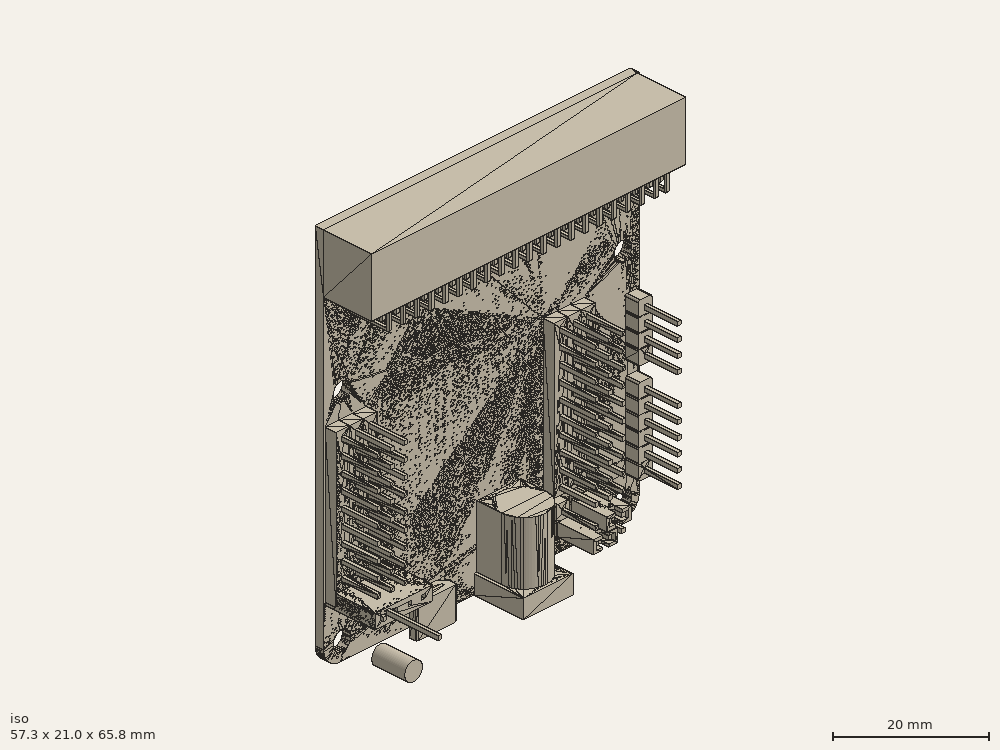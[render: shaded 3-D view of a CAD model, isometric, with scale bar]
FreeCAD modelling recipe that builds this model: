
FCSTD DOCUMENT  (FreeCAD 0.20R29603 (Git))
Label: PlacaExpansion
License: All rights reserved
LicenseURL: http://en.wikipedia.org/wiki/All_rights_reserved
objects: Part::Box×66, Part::MultiFuse×27, Part::Fillet×22, Part::FeaturePython×16, Part::Cut×16, Part::Cylinder×8, Part::Chamfer×8
note: 147 computed .brp shape members not serialized (recipe doc carries the construction recipe); baked Part::Feature solids carry a one-line shape summary decoded from their .brp

FEATURE [Part::Box] Box103  label="Extensor002"
  AttacherType = Attacher::AttachEngine3D
  Height = 65.33
  Length = 1.54
  Placement = pos=(30,-28,3) rot=(0,0,1;1.5708rad)
  Width = 57.33
FEATURE [Part::Box] Box202  label="Cubo189"
  AttacherType = Attacher::AttachEngine3D
  Height = 10
  Length = 57
  Placement = pos=(-27.33,-36.75,58.33) rot=(0,0,1;0rad)
  Width = 8.8
FEATURE [Part::Box] Box207  label="Cubo194"
  AttacherType = Attacher::AttachEngine3D
  Height = 26
  Length = 2.5
  Placement = pos=(-27,-30,13) rot=(0,0,1;0rad)
  Width = 2.5
FEATURE [Part::Box] Box208  label="Cubo195"
  AttacherType = Attacher::AttachEngine3D
  Height = 26
  Length = 2.5
  Placement = pos=(-24.5,-30,13) rot=(0,0,1;0rad)
  Width = 2.5
FEATURE [Part::Box] Box209  label="Cubo196"
  AttacherType = Attacher::AttachEngine3D
  Height = 26
  Length = 2.5
  Placement = pos=(-22,-30,13) rot=(0,0,1;0rad)
  Width = 2.5
FEATURE [Part::Box] Box210  label="Cubo197"
  AttacherType = Attacher::AttachEngine3D
  Height = 11
  Length = 0.6
  Placement = pos=(-26,-25.5,14) rot=(1,0,0;1.5708rad)
  Width = 0.7
FEATURE [Part::FeaturePython] Array003  # Draft array (typed FeaturePython)
  AlwaysSyncPlacement = false
  Angle = 360
  ArrayType = 0
  Axis = (0,0,1)
  Base = -> Box210
  Center = (0,0,0)
  Count = 30
  ExpandArray = false
  Fuse = false
  IntervalAxis = (0,0,0)
  IntervalX = (2.45,0,0)
  IntervalY = (0,100,0)
  IntervalZ = (0,0,2.6)
  NumberCircles = 3
  NumberPolar = 5
  NumberX = 3
  NumberY = 1
  NumberZ = 10
  PlacementList = 30 placements: [(-26,-25.5,14),(-26,-25.5,16.6),(-26,-25.5,19.2),(-26,-25.5,21.8),(-26,-25.5,24.4),(-26,-25.5,27),(-26,-25.5,29.6),(-26,-25.5,32.2),(-26,-25.5,34.8),(-26,-25.5,37.4),(-23.55,-25.5,14),(-23.55,-25.5,16.6),(-23.55,-25.5,19.2),(-23.55,-25.5,21.8),(-23.55,-25.5,24.4),(-23.55,-25.5,27),(-23.55,-25.5,29.6),(-23.55,-25.5,32.2),(-23.55,-25.5,34.8),(-23.55,-25.5,37.4),(-21.1,-25.5,14),(-21.1,-25.5,16.6),+8 more]
  RadialDistance = 50
  ScaleList = (30) [(1,1,1),(1,1,1),(1,1,1),(1,1,1),(1,1,1),(1,1,1),(1,1,1),(1,1,1),(1,1,1),(1,1,1),(1,1,1),(1,1,1),(1,1,1),(1,1,1),(1,1,1),(1,1,1),(1,1,1),(1,1,1),+12 more]
  Symmetry = 1
  TangentialDistance = 25
FEATURE [Part::Cylinder] Cylinder189  label="Cilindro189"
  Angle = 360
  AttacherType = Attacher::AttachEngine3D
  FirstAngle = 0
  Height = 6
  Placement = pos=(-24,-24,6) rot=(1,0,0;1.5708rad)
  Radius = 1.6
  SecondAngle = 0
FEATURE [Part::FeaturePython] Array001  # Draft array (typed FeaturePython)
  AlwaysSyncPlacement = false
  Angle = 360
  ArrayType = 0
  Axis = (0,0,1)
  Base = -> Cylinder189
  Center = (0,0,0)
  Count = 4
  ExpandArray = false
  Fuse = false
  IntervalAxis = (0,0,0)
  IntervalX = (51,0,0)
  IntervalY = (0,100,0)
  IntervalZ = (0,0,37)
  NumberCircles = 3
  NumberPolar = 5
  NumberX = 2
  NumberY = 1
  NumberZ = 2
  PlacementList = 4 placements: [(-24,-24,6),(-24,-24,43),(27,-24,6),(27,-24,43)]
  RadialDistance = 50
  ScaleList = (4) [(1,1,1),(1,1,1),(1,1,1),(1,1,1)]
  Symmetry = 1
  TangentialDistance = 25
FEATURE [Part::Fillet] Fillet160
  Base = -> Box103
  Edges = 2 edges r=3: [Edge9,Edge11]
FEATURE [Part::Cut] Cut258
  Base = -> Fillet160
  Tool = -> Array001
FEATURE [Part::MultiFuse] Fusion135  label="Conector_Pines001"
  Placement = pos=(-7,0,52) rot=(0,1,0;3.14159rad)
  Shapes = -> [Box207,Box208,Box209,Array003]
FEATURE [Part::MultiFuse] Fusion136
  Shapes = -> [Cut258,Box202]
FEATURE [Part::Box] Box211  label="Cubo198"
  AttacherType = Attacher::AttachEngine3D
  Height = 26
  Length = 2.5
  Placement = pos=(-27,-30,13) rot=(0,0,1;0rad)
  Width = 2.5
FEATURE [Part::Box] Box212  label="Cubo199"
  AttacherType = Attacher::AttachEngine3D
  Height = 26
  Length = 2.5
  Placement = pos=(-24.5,-30,13) rot=(0,0,1;0rad)
  Width = 2.5
FEATURE [Part::Box] Box213  label="Cubo200"
  AttacherType = Attacher::AttachEngine3D
  Height = 26
  Length = 2.5
  Placement = pos=(-22,-30,13) rot=(0,0,1;0rad)
  Width = 2.5
FEATURE [Part::Box] Box214  label="Cubo201"
  AttacherType = Attacher::AttachEngine3D
  Height = 11
  Length = 0.6
  Placement = pos=(-26,-25.5,14) rot=(1,0,0;1.5708rad)
  Width = 0.7
FEATURE [Part::FeaturePython] Array004  # Draft array (typed FeaturePython)
  AlwaysSyncPlacement = false
  Angle = 360
  ArrayType = 0
  Axis = (0,0,1)
  Base = -> Box214
  Center = (0,0,0)
  Count = 30
  ExpandArray = false
  Fuse = false
  IntervalAxis = (0,0,0)
  IntervalX = (2.45,0,0)
  IntervalY = (0,100,0)
  IntervalZ = (0,0,2.6)
  NumberCircles = 3
  NumberPolar = 5
  NumberX = 3
  NumberY = 1
  NumberZ = 10
  PlacementList = <same value as first occurrence — deduplicated (x4 in doc)>
  RadialDistance = 50
  ScaleList = (30) [(1,1,1),(1,1,1),(1,1,1),(1,1,1),(1,1,1),(1,1,1),(1,1,1),(1,1,1),(1,1,1),(1,1,1),(1,1,1),(1,1,1),(1,1,1),(1,1,1),(1,1,1),(1,1,1),(1,1,1),(1,1,1),+12 more]
  Symmetry = 1
  TangentialDistance = 25
FEATURE [Part::MultiFuse] Fusion137  label="Conector_Pines002"
  Placement = pos=(-46.6,0,52) rot=(0,1,0;3.14159rad)
  Shapes = -> [Box211,Box212,Box213,Array004]
FEATURE [Part::MultiFuse] Fusion  label="PlacaExpansión"
  Placement = pos=(-1,10,0) rot=(0,0,1;0rad)
  Shapes = -> [Fusion136,Fusion137,Fusion135]
FEATURE [Part::Box] Box292  label="Cubo277"
  AttacherType = Attacher::AttachEngine3D
  Height = 6.5
  Length = 0.5
  Placement = pos=(27,-25,54) rot=(0,0,1;0rad)
  Width = 0.5
FEATURE [Part::Box] Box293  label="Cubo278"
  AttacherType = Attacher::AttachEngine3D
  Height = 6.5
  Length = 0.5
  Placement = pos=(27,-24.5,54.5) rot=(-1,0,0;1.5708rad)
  Width = 0.5
FEATURE [Part::Box] Box294  label="Cubo279"
  AttacherType = Attacher::AttachEngine3D
  Height = 6.5
  Length = 0.5
  Placement = pos=(27,-25,54) rot=(0,0,1;0rad)
  Width = 0.5
FEATURE [Part::Box] Box295  label="Cubo280"
  AttacherType = Attacher::AttachEngine3D
  Height = 6.5
  Length = 0.5
  Placement = pos=(27,-24.5,54.5) rot=(-1,0,0;1.5708rad)
  Width = 0.5
FEATURE [Part::Box] Box296  label="Cubo281"
  AttacherType = Attacher::AttachEngine3D
  Height = 10.5
  Length = 2.5
  Placement = pos=(-28,-27,15) rot=(0,1,0;1.5708rad)
  Width = 9
FEATURE [Part::Box] Box297  label="Cubo282"
  AttacherType = Attacher::AttachEngine3D
  Height = 5
  Length = 0.6
  Placement = pos=(-27,-22.5,13.5) rot=(1,0,0;1.5708rad)
  Width = 0.7
FEATURE [Part::FeaturePython] Array009  # Draft array (typed FeaturePython)
  AlwaysSyncPlacement = false
  Angle = 360
  ArrayType = 0
  Axis = (0,0,1)
  Base = -> Box297
  Center = (0,0,0)
  Count = 4
  ExpandArray = false
  Fuse = false
  IntervalAxis = (0,0,0)
  IntervalX = (2.5,0,0)
  IntervalY = (0,100,0)
  IntervalZ = (0,0,100)
  NumberCircles = 3
  NumberPolar = 5
  NumberX = 4
  NumberY = 1
  NumberZ = 1
  PlacementList = 4 placements: arithmetic series from (-27,-22.5,13.5) step (2.5,0,0) to (-19.5,-22.5,13.5)
  RadialDistance = 50
  ScaleList = (4) [(1,1,1),(1,1,1),(1,1,1),(1,1,1)]
  Symmetry = 1
  TangentialDistance = 25
FEATURE [Part::Box] Box298  label="Cubo283"
  AttacherType = Attacher::AttachEngine3D
  Height = 3.2
  Length = 9
  Width = 9
FEATURE [Part::Box] Box299  label="Cubo284"
  AttacherType = Attacher::AttachEngine3D
  Height = 13.8
  Length = 8
  Placement = pos=(0.5,4.5,0) rot=(0,0,1;0rad)
  Width = 4.5
FEATURE [Part::Box] Box300  label="Cubo285"
  AttacherType = Attacher::AttachEngine3D
  Height = 5.5
  Length = 7.3
  Width = 2.6
FEATURE [Part::Box] Box301  label="Cubo286"
  AttacherType = Attacher::AttachEngine3D
  Height = 5
  Length = 7
  Width = 2.3
FEATURE [Part::Box] Box302  label="Cubo287"
  AttacherType = Attacher::AttachEngine3D
  Height = 4
  Length = 5
  Placement = pos=(1,1,1.5) rot=(0,0,1;0rad)
  Width = 0.5
FEATURE [Part::Box] Box303  label="Cubo288"
  AttacherType = Attacher::AttachEngine3D
  Height = 2.6
  Length = 2.4
  Placement = pos=(11.5,-20.4,9.6) rot=(0,0,1;0rad)
  Width = 2.4
FEATURE [Part::Box] Box304  label="Cubo289"
  AttacherType = Attacher::AttachEngine3D
  Height = 11
  Length = 0.6
  Placement = pos=(12.5,-15.5,10.5) rot=(1,0,0;1.5708rad)
  Width = 0.7
FEATURE [Part::Box] Box305  label="Cubo290"
  AttacherType = Attacher::AttachEngine3D
  Height = 2.2
  Length = 4.4
  Placement = pos=(14.2,-26.9,9.8) rot=(0,0,1;0rad)
  Width = 6.5
FEATURE [Part::Box] Box306  label="Cubo291"
  AttacherType = Attacher::AttachEngine3D
  Height = 1.2
  Length = 3.4
  Placement = pos=(14.7,-27,10.26) rot=(0,0,1;0rad)
  Width = 6.5
FEATURE [Part::Box] Box307  label="Cubo292"
  AttacherType = Attacher::AttachEngine3D
  Height = 1.2
  Length = 3.4
  Placement = pos=(15.8,-32,13) rot=(0,1,0;1.5708rad)
  Width = 6.5
FEATURE [Part::Box] Box308  label="Cubo293"
  AttacherType = Attacher::AttachEngine3D
  Height = 2.2
  Length = 4.4
  Placement = pos=(14.2,-26.9,9.8) rot=(0,0,1;0rad)
  Width = 6.5
FEATURE [Part::Box] Box309  label="Cubo294"
  AttacherType = Attacher::AttachEngine3D
  Height = 1.2
  Length = 3.4
  Placement = pos=(14.7,-27,10.26) rot=(0,0,1;0rad)
  Width = 6.5
FEATURE [Part::Box] Box310  label="Cubo295"
  AttacherType = Attacher::AttachEngine3D
  Height = 1.2
  Length = 3.4
  Placement = pos=(15.8,-32,13) rot=(0,1,0;1.5708rad)
  Width = 6.5
FEATURE [Part::Cut] Cut345  label="4PinesHembra"
  Base = -> Box296
  Tool = -> Array009
FEATURE [Part::Cut] Cut348
  Base = -> Box305
  Tool = -> Box306
FEATURE [Part::Cut] Cut349  label="ConectorUnionPines"
  Base = -> Cut348
  Tool = -> Box307
FEATURE [Part::Cut] Cut350
  Base = -> Box308
  Tool = -> Box309
FEATURE [Part::Cut] Cut351  label="ConectorUnionPines001"
  Base = -> Cut350
  Placement = pos=(-2.4,0,-2.4) rot=(0,0,1;0rad)
  Tool = -> Box310
FEATURE [Part::Cylinder] Cylinder263  label="Cilindro263"
  Angle = 360
  AttacherType = Attacher::AttachEngine3D
  FirstAngle = 0
  Height = 13.8
  Placement = pos=(4.5,4.5,0) rot=(0,0,1;0rad)
  Radius = 4
  SecondAngle = 0
FEATURE [Part::Cylinder] Cylinder264  label="Cilindro264"
  Angle = 360
  AttacherType = Attacher::AttachEngine3D
  FirstAngle = 0
  Height = 12.8
  Placement = pos=(4.5,4.5,0) rot=(0,0,1;0rad)
  Radius = 3
  SecondAngle = 0
FEATURE [Part::Cylinder] Cylinder265  label="Cilindro265"
  Angle = 360
  AttacherType = Attacher::AttachEngine3D
  FirstAngle = 0
  Height = 13.5
  Radius = 0.5
  SecondAngle = 0
FEATURE [Part::Fillet] Fillet221
  Base = -> Cylinder265
  Edges = 1 edges r=0.25: [Edge2]
  Placement = pos=(4.5,4.5,0) rot=(0,0,1;0rad)
FEATURE [Part::Fillet] Fillet222
  Base = -> Box300
  Edges = 2 edges r=0.3: [Edge1,Edge5]
FEATURE [Part::Chamfer] Chamfer041
  Base = -> Fillet222
  Edges = 1 edges r=1.3: [Edge13]
FEATURE [Part::Chamfer] Chamfer042
  Base = -> Chamfer041
  Edges = 1 edges r=1.3: [Edge16]
FEATURE [Part::Fillet] Fillet223
  Base = -> Box301
  Edges = 2 edges r=0.3: [Edge1,Edge5]
FEATURE [Part::Chamfer] Chamfer043
  Base = -> Fillet223
  Edges = 1 edges r=1.3: [Edge13]
FEATURE [Part::Chamfer] Chamfer044
  Base = -> Chamfer043
  Edges = 1 edges r=1.3: [Edge16]
  Placement = pos=(0.15,0.15,0) rot=(0,0,1;0rad)
FEATURE [Part::Cut] Cut347
  Base = -> Chamfer042
  Tool = -> Chamfer044
FEATURE [Part::Fillet] Fillet224  label="Base_Conector"
  Base = -> Box303
  Edges = 4 edges r=0.3: [Edge2,Edge4,Edge6,Edge8]
FEATURE [Part::MultiFuse] Fusion199
  Shapes = -> [Box292,Box293]
FEATURE [Part::Fillet] Fillet217
  Base = -> Fusion199
  Edges = 1 edges r=0.2: [Edge6]
FEATURE [Part::Fillet] Fillet218
  Base = -> Fillet217
  Edges = 1 edges r=0.2: [Edge16]
  Placement = pos=(-1.2,0,2) rot=(0,0,1;0rad)
FEATURE [Part::MultiFuse] Fusion200
  Shapes = -> [Box294,Box295]
FEATURE [Part::Fillet] Fillet219
  Base = -> Fusion200
  Edges = 1 edges r=0.2: [Edge6]
FEATURE [Part::Fillet] Fillet220
  Base = -> Fillet219
  Edges = 1 edges r=0.2: [Edge16]
FEATURE [Part::MultiFuse] Fusion201
  Shapes = -> [Fillet220,Fillet218]
FEATURE [Part::FeaturePython] Array008  label="ConexionesPrincipales"  # Draft array (typed FeaturePython)
  AlwaysSyncPlacement = false
  Angle = 360
  ArrayType = 0
  Axis = (0,0,1)
  Base = -> Fusion201
  Center = (0,0,0)
  Count = 20
  ExpandArray = false
  Fuse = false
  IntervalAxis = (0,0,0)
  IntervalX = (-2.55,0,0)
  IntervalY = (0,100,0)
  IntervalZ = (0,0,100)
  NumberCircles = 3
  NumberPolar = 5
  NumberX = 20
  NumberY = 1
  NumberZ = 1
  Placement = pos=(-2,0,0) rot=(0,0,1;0rad)
  PlacementList = 20 placements: arithmetic series from (0,0,0) step (-2.55,0,0) to (-48.45,0,0)
  RadialDistance = 50
  ScaleList = (20) [(1,1,1),(1,1,1),(1,1,1),(1,1,1),(1,1,1),(1,1,1),(1,1,1),(1,1,1),(1,1,1),(1,1,1),(1,1,1),(1,1,1),(1,1,1),(1,1,1),(1,1,1),(1,1,1),(1,1,1),(1,1,1),+2 more]
  Symmetry = 1
  TangentialDistance = 25
FEATURE [Part::MultiFuse] Fusion202
  Shapes = -> [Box298,Cylinder263,Box299]
FEATURE [Part::Cut] Cut346
  Base = -> Fusion202
  Tool = -> Cylinder264
FEATURE [Part::MultiFuse] Fusion203  label="Conector_Vcc"
  Placement = pos=(-1,-27,3) rot=(0,0,1;0rad)
  Shapes = -> [Cut346,Fillet221]
FEATURE [Part::MultiFuse] Fusion204  label="Conector_MicroUSB"
  Placement = pos=(-14,-20.6,2.5) rot=(0,0,1;0rad)
  Shapes = -> [Box302,Cut347]
FEATURE [Part::MultiFuse] Fusion205  label="Conector_Macho_Negro"
  Shapes = -> [Fillet224,Box304]
FEATURE [Part::FeaturePython] Array010  # Draft array (typed FeaturePython)
  AlwaysSyncPlacement = false
  Angle = 360
  ArrayType = 0
  Axis = (0,0,1)
  Base = -> Fusion205
  Center = (0,0,0)
  Count = 6
  ExpandArray = false
  Fuse = false
  IntervalAxis = (0,0,0)
  IntervalX = (2.4,0,0)
  IntervalY = (0,100,0)
  IntervalZ = (0,0,-2.4)
  NumberCircles = 3
  NumberPolar = 5
  NumberX = 3
  NumberY = 1
  NumberZ = 2
  PlacementList = 6 placements: [(0,0,0),(0,0,-2.4),(2.4,0,0),(2.4,0,-2.4),(4.8,0,0),(4.8,0,-2.4)]
  RadialDistance = 50
  ScaleList = (6) [(1,1,1),(1,1,1),(1,1,1),(1,1,1),(1,1,1),(1,1,1)]
  Symmetry = 1
  TangentialDistance = 25
FEATURE [Part::Box] Box311  label="Cubo296"
  AttacherType = Attacher::AttachEngine3D
  Height = 2.6
  Length = 2.4
  Placement = pos=(11.5,-20.4,9.6) rot=(0,0,1;0rad)
  Width = 2.4
FEATURE [Part::Box] Box312  label="Cubo297"
  AttacherType = Attacher::AttachEngine3D
  Height = 11
  Length = 0.6
  Placement = pos=(12.5,-15.5,10.5) rot=(1,0,0;1.5708rad)
  Width = 0.7
FEATURE [Part::Fillet] Fillet225  label="Base_Conector001"
  Base = -> Box311
  Edges = 4 edges r=0.3: [Edge2,Edge4,Edge6,Edge8]
FEATURE [Part::MultiFuse] Fusion206  label="Conector_MachoAmarillo"
  Placement = pos=(15,0,0) rot=(0,0,1;0rad)
  Shapes = -> [Box312,Fillet225]
FEATURE [Part::Box] Box313  label="Cubo298"
  AttacherType = Attacher::AttachEngine3D
  Height = 2.6
  Length = 2.4
  Placement = pos=(11.5,-20.4,9.6) rot=(0,0,1;0rad)
  Width = 2.4
FEATURE [Part::FeaturePython] Array  # Draft array (typed FeaturePython)
  AlwaysSyncPlacement = false
  Angle = 360
  ArrayType = 0
  Axis = (0,0,1)
  Base = -> Fusion206
  Center = (0,0,0)
  Count = 6
  ExpandArray = false
  Fuse = false
  IntervalAxis = (0,0,0)
  IntervalX = (100,0,0)
  IntervalY = (0,100,0)
  IntervalZ = (0,0,2.4)
  NumberCircles = 3
  NumberPolar = 5
  NumberX = 1
  NumberY = 1
  NumberZ = 6
  PlacementList = 6 placements: arithmetic series from (15,0,0) step (0,0,2.4) to (15,0,12)
  RadialDistance = 50
  ScaleList = (6) [(1,1,1),(1,1,1),(1,1,1),(1,1,1),(1,1,1),(1,1,1)]
  Symmetry = 1
  TangentialDistance = 25
FEATURE [Part::Box] Box314  label="Cubo299"
  AttacherType = Attacher::AttachEngine3D
  Height = 11
  Length = 0.6
  Placement = pos=(22.5,-15.5,10.5) rot=(1,0,0;1.5708rad)
  Width = 0.7
FEATURE [Part::Fillet] Fillet226  label="Base_Conector002"
  Base = -> Box313
  Edges = 4 edges r=0.3: [Edge2,Edge4,Edge6,Edge8]
  Placement = pos=(10,0,0) rot=(0,0,1;0rad)
FEATURE [Part::MultiFuse] Fusion207
  Placement = pos=(5,0,17) rot=(0,0,1;0rad)
  Shapes = -> [Fillet226,Box314]
FEATURE [Part::FeaturePython] Array011  # Draft array (typed FeaturePython)
  AlwaysSyncPlacement = false
  Angle = 360
  ArrayType = 0
  Axis = (0,0,1)
  Base = -> Fusion207
  Center = (0,0,0)
  Count = 4
  ExpandArray = false
  Fuse = false
  IntervalAxis = (0,0,0)
  IntervalX = (100,0,0)
  IntervalY = (0,100,0)
  IntervalZ = (0,0,2.4)
  NumberCircles = 3
  NumberPolar = 5
  NumberX = 1
  NumberY = 1
  NumberZ = 4
  PlacementList = 4 placements: arithmetic series from (5,0,17) step (0,0,2.4) to (5,0,24.2)
  RadialDistance = 50
  ScaleList = (4) [(1,1,1),(1,1,1),(1,1,1),(1,1,1)]
  Symmetry = 1
  TangentialDistance = 25
FEATURE [Part::Box] Box315  label="Extensor003"
  AttacherType = Attacher::AttachEngine3D
  Height = 65.33
  Length = 1.54
  Placement = pos=(30,-28,3) rot=(0,0,1;1.5708rad)
  Width = 57.33
FEATURE [Part::Box] Box316  label="Cubo300"
  AttacherType = Attacher::AttachEngine3D
  Height = 10
  Length = 57
  Placement = pos=(-27.33,-36.75,58.33) rot=(0,0,1;0rad)
  Width = 8.8
FEATURE [Part::Box] Box317  label="Cubo301"
  AttacherType = Attacher::AttachEngine3D
  Height = 26
  Length = 2.5
  Placement = pos=(-27,-30,13) rot=(0,0,1;0rad)
  Width = 2.5
FEATURE [Part::Box] Box318  label="Cubo302"
  AttacherType = Attacher::AttachEngine3D
  Height = 26
  Length = 2.5
  Placement = pos=(-24.5,-30,13) rot=(0,0,1;0rad)
  Width = 2.5
FEATURE [Part::Box] Box319  label="Cubo303"
  AttacherType = Attacher::AttachEngine3D
  Height = 26
  Length = 2.5
  Placement = pos=(-22,-30,13) rot=(0,0,1;0rad)
  Width = 2.5
FEATURE [Part::Box] Box320  label="Cubo304"
  AttacherType = Attacher::AttachEngine3D
  Height = 11
  Length = 0.6
  Placement = pos=(-26,-25.5,14) rot=(1,0,0;1.5708rad)
  Width = 0.7
FEATURE [Part::FeaturePython] Array014  # Draft array (typed FeaturePython)
  AlwaysSyncPlacement = false
  Angle = 360
  ArrayType = 0
  Axis = (0,0,1)
  Base = -> Box320
  Center = (0,0,0)
  Count = 30
  ExpandArray = false
  Fuse = false
  IntervalAxis = (0,0,0)
  IntervalX = (2.45,0,0)
  IntervalY = (0,100,0)
  IntervalZ = (0,0,2.6)
  NumberCircles = 3
  NumberPolar = 5
  NumberX = 3
  NumberY = 1
  NumberZ = 10
  PlacementList = <same value as first occurrence — deduplicated (x4 in doc)>
  RadialDistance = 50
  ScaleList = (30) [(1,1,1),(1,1,1),(1,1,1),(1,1,1),(1,1,1),(1,1,1),(1,1,1),(1,1,1),(1,1,1),(1,1,1),(1,1,1),(1,1,1),(1,1,1),(1,1,1),(1,1,1),(1,1,1),(1,1,1),(1,1,1),+12 more]
  Symmetry = 1
  TangentialDistance = 25
FEATURE [Part::Box] Box321  label="Cubo305"
  AttacherType = Attacher::AttachEngine3D
  Height = 26
  Length = 2.5
  Placement = pos=(-27,-30,13) rot=(0,0,1;0rad)
  Width = 2.5
FEATURE [Part::Box] Box322  label="Cubo306"
  AttacherType = Attacher::AttachEngine3D
  Height = 26
  Length = 2.5
  Placement = pos=(-24.5,-30,13) rot=(0,0,1;0rad)
  Width = 2.5
FEATURE [Part::Box] Box323  label="Cubo307"
  AttacherType = Attacher::AttachEngine3D
  Height = 26
  Length = 2.5
  Placement = pos=(-22,-30,13) rot=(0,0,1;0rad)
  Width = 2.5
FEATURE [Part::Box] Box324  label="Cubo308"
  AttacherType = Attacher::AttachEngine3D
  Height = 11
  Length = 0.6
  Placement = pos=(-26,-25.5,14) rot=(1,0,0;1.5708rad)
  Width = 0.7
FEATURE [Part::FeaturePython] Array015  # Draft array (typed FeaturePython)
  AlwaysSyncPlacement = false
  Angle = 360
  ArrayType = 0
  Axis = (0,0,1)
  Base = -> Box324
  Center = (0,0,0)
  Count = 30
  ExpandArray = false
  Fuse = false
  IntervalAxis = (0,0,0)
  IntervalX = (2.45,0,0)
  IntervalY = (0,100,0)
  IntervalZ = (0,0,2.6)
  NumberCircles = 3
  NumberPolar = 5
  NumberX = 3
  NumberY = 1
  NumberZ = 10
  PlacementList = <same value as first occurrence — deduplicated (x4 in doc)>
  RadialDistance = 50
  ScaleList = (30) [(1,1,1),(1,1,1),(1,1,1),(1,1,1),(1,1,1),(1,1,1),(1,1,1),(1,1,1),(1,1,1),(1,1,1),(1,1,1),(1,1,1),(1,1,1),(1,1,1),(1,1,1),(1,1,1),(1,1,1),(1,1,1),+12 more]
  Symmetry = 1
  TangentialDistance = 25
FEATURE [Part::Box] Box325  label="Cubo309"
  AttacherType = Attacher::AttachEngine3D
  Height = 6.5
  Length = 0.5
  Placement = pos=(27,-25,54) rot=(0,0,1;0rad)
  Width = 0.5
FEATURE [Part::Box] Box326  label="Cubo310"
  AttacherType = Attacher::AttachEngine3D
  Height = 6.5
  Length = 0.5
  Placement = pos=(27,-24.5,54.5) rot=(-1,0,0;1.5708rad)
  Width = 0.5
FEATURE [Part::Box] Box327  label="Cubo311"
  AttacherType = Attacher::AttachEngine3D
  Height = 6.5
  Length = 0.5
  Placement = pos=(27,-25,54) rot=(0,0,1;0rad)
  Width = 0.5
FEATURE [Part::Box] Box328  label="Cubo312"
  AttacherType = Attacher::AttachEngine3D
  Height = 6.5
  Length = 0.5
  Placement = pos=(27,-24.5,54.5) rot=(-1,0,0;1.5708rad)
  Width = 0.5
FEATURE [Part::Box] Box329  label="Cubo313"
  AttacherType = Attacher::AttachEngine3D
  Height = 10.5
  Length = 2.5
  Placement = pos=(-28,-27,15) rot=(0,1,0;1.5708rad)
  Width = 9
FEATURE [Part::Box] Box330  label="Cubo314"
  AttacherType = Attacher::AttachEngine3D
  Height = 5
  Length = 0.6
  Placement = pos=(-27,-22.5,13.5) rot=(1,0,0;1.5708rad)
  Width = 0.7
FEATURE [Part::FeaturePython] Array017  # Draft array (typed FeaturePython)
  AlwaysSyncPlacement = false
  Angle = 360
  ArrayType = 0
  Axis = (0,0,1)
  Base = -> Box330
  Center = (0,0,0)
  Count = 4
  ExpandArray = false
  Fuse = false
  IntervalAxis = (0,0,0)
  IntervalX = (2.5,0,0)
  IntervalY = (0,100,0)
  IntervalZ = (0,0,100)
  NumberCircles = 3
  NumberPolar = 5
  NumberX = 4
  NumberY = 1
  NumberZ = 1
  PlacementList = 4 placements: arithmetic series from (-27,-22.5,13.5) step (2.5,0,0) to (-19.5,-22.5,13.5)
  RadialDistance = 50
  ScaleList = (4) [(1,1,1),(1,1,1),(1,1,1),(1,1,1)]
  Symmetry = 1
  TangentialDistance = 25
FEATURE [Part::Box] Box331  label="Cubo315"
  AttacherType = Attacher::AttachEngine3D
  Height = 3.2
  Length = 9
  Width = 9
FEATURE [Part::Box] Box332  label="Cubo316"
  AttacherType = Attacher::AttachEngine3D
  Height = 13.8
  Length = 8
  Placement = pos=(0.5,4.5,0) rot=(0,0,1;0rad)
  Width = 4.5
FEATURE [Part::Box] Box333  label="Cubo317"
  AttacherType = Attacher::AttachEngine3D
  Height = 5.5
  Length = 7.3
  Width = 2.6
FEATURE [Part::Box] Box334  label="Cubo318"
  AttacherType = Attacher::AttachEngine3D
  Height = 5
  Length = 7
  Width = 2.3
FEATURE [Part::Box] Box335  label="Cubo319"
  AttacherType = Attacher::AttachEngine3D
  Height = 4
  Length = 5
  Placement = pos=(1,1,1.5) rot=(0,0,1;0rad)
  Width = 0.5
FEATURE [Part::Box] Box336  label="Cubo320"
  AttacherType = Attacher::AttachEngine3D
  Height = 2.6
  Length = 2.4
  Placement = pos=(11.5,-20.4,9.6) rot=(0,0,1;0rad)
  Width = 2.4
FEATURE [Part::Box] Box337  label="Cubo321"
  AttacherType = Attacher::AttachEngine3D
  Height = 11
  Length = 0.6
  Placement = pos=(12.5,-15.5,10.5) rot=(1,0,0;1.5708rad)
  Width = 0.7
FEATURE [Part::Box] Box338  label="Cubo322"
  AttacherType = Attacher::AttachEngine3D
  Height = 2.2
  Length = 4.4
  Placement = pos=(14.2,-26.9,9.8) rot=(0,0,1;0rad)
  Width = 6.5
FEATURE [Part::Box] Box339  label="Cubo323"
  AttacherType = Attacher::AttachEngine3D
  Height = 1.2
  Length = 3.4
  Placement = pos=(14.7,-27,10.26) rot=(0,0,1;0rad)
  Width = 6.5
FEATURE [Part::Box] Box340  label="Cubo324"
  AttacherType = Attacher::AttachEngine3D
  Height = 1.2
  Length = 3.4
  Placement = pos=(15.8,-32,13) rot=(0,1,0;1.5708rad)
  Width = 6.5
FEATURE [Part::Box] Box341  label="Cubo325"
  AttacherType = Attacher::AttachEngine3D
  Height = 2.2
  Length = 4.4
  Placement = pos=(14.2,-26.9,9.8) rot=(0,0,1;0rad)
  Width = 6.5
FEATURE [Part::Box] Box342  label="Cubo326"
  AttacherType = Attacher::AttachEngine3D
  Height = 1.2
  Length = 3.4
  Placement = pos=(14.7,-27,10.26) rot=(0,0,1;0rad)
  Width = 6.5
FEATURE [Part::Box] Box343  label="Cubo327"
  AttacherType = Attacher::AttachEngine3D
  Height = 1.2
  Length = 3.4
  Placement = pos=(15.8,-32,13) rot=(0,1,0;1.5708rad)
  Width = 6.5
FEATURE [Part::Box] Box344  label="Cubo328"
  AttacherType = Attacher::AttachEngine3D
  Height = 2.6
  Length = 2.4
  Placement = pos=(11.5,-20.4,9.6) rot=(0,0,1;0rad)
  Width = 2.4
FEATURE [Part::Box] Box345  label="Cubo329"
  AttacherType = Attacher::AttachEngine3D
  Height = 11
  Length = 0.6
  Placement = pos=(12.5,-15.5,10.5) rot=(1,0,0;1.5708rad)
  Width = 0.7
FEATURE [Part::Box] Box346  label="Cubo330"
  AttacherType = Attacher::AttachEngine3D
  Height = 2.6
  Length = 2.4
  Placement = pos=(11.5,-20.4,9.6) rot=(0,0,1;0rad)
  Width = 2.4
FEATURE [Part::Box] Box347  label="Cubo331"
  AttacherType = Attacher::AttachEngine3D
  Height = 11
  Length = 0.6
  Placement = pos=(22.5,-15.5,10.5) rot=(1,0,0;1.5708rad)
  Width = 0.7
FEATURE [Part::Cut] Cut353  label="4PinesHembra001"
  Base = -> Box329
  Tool = -> Array017
FEATURE [Part::Cut] Cut356
  Base = -> Box338
  Tool = -> Box339
FEATURE [Part::Cut] Cut357  label="ConectorUnionPines002"
  Base = -> Cut356
  Tool = -> Box340
FEATURE [Part::Cut] Cut358
  Base = -> Box341
  Tool = -> Box342
FEATURE [Part::Cut] Cut359  label="ConectorUnionPines003"
  Base = -> Cut358
  Placement = pos=(-2.4,0,-2.4) rot=(0,0,1;0rad)
  Tool = -> Box343
FEATURE [Part::Cylinder] Cylinder266  label="Cilindro266"
  Angle = 360
  AttacherType = Attacher::AttachEngine3D
  FirstAngle = 0
  Height = 6
  Placement = pos=(-24,-24,6) rot=(1,0,0;1.5708rad)
  Radius = 1.6
  SecondAngle = 0
FEATURE [Part::FeaturePython] Array013  # Draft array (typed FeaturePython)
  AlwaysSyncPlacement = false
  Angle = 360
  ArrayType = 0
  Axis = (0,0,1)
  Base = -> Cylinder266
  Center = (0,0,0)
  Count = 4
  ExpandArray = false
  Fuse = false
  IntervalAxis = (0,0,0)
  IntervalX = (51,0,0)
  IntervalY = (0,100,0)
  IntervalZ = (0,0,37)
  NumberCircles = 3
  NumberPolar = 5
  NumberX = 2
  NumberY = 1
  NumberZ = 2
  PlacementList = 4 placements: [(-24,-24,6),(-24,-24,43),(27,-24,6),(27,-24,43)]
  RadialDistance = 50
  ScaleList = (4) [(1,1,1),(1,1,1),(1,1,1),(1,1,1)]
  Symmetry = 1
  TangentialDistance = 25
FEATURE [Part::Cylinder] Cylinder267  label="Cilindro267"
  Angle = 360
  AttacherType = Attacher::AttachEngine3D
  FirstAngle = 0
  Height = 13.8
  Placement = pos=(4.5,4.5,0) rot=(0,0,1;0rad)
  Radius = 4
  SecondAngle = 0
FEATURE [Part::Cylinder] Cylinder268  label="Cilindro268"
  Angle = 360
  AttacherType = Attacher::AttachEngine3D
  FirstAngle = 0
  Height = 12.8
  Placement = pos=(4.5,4.5,0) rot=(0,0,1;0rad)
  Radius = 3
  SecondAngle = 0
FEATURE [Part::Cylinder] Cylinder269  label="Cilindro269"
  Angle = 360
  AttacherType = Attacher::AttachEngine3D
  FirstAngle = 0
  Height = 13.5
  Radius = 0.5
  SecondAngle = 0
FEATURE [Part::Fillet] Fillet227
  Base = -> Box315
  Edges = 2 edges r=3: [Edge9,Edge11]
FEATURE [Part::Cut] Cut352
  Base = -> Fillet227
  Tool = -> Array013
FEATURE [Part::Fillet] Fillet232
  Base = -> Cylinder269
  Edges = 1 edges r=0.25: [Edge2]
  Placement = pos=(4.5,4.5,0) rot=(0,0,1;0rad)
FEATURE [Part::Fillet] Fillet233
  Base = -> Box333
  Edges = 2 edges r=0.3: [Edge1,Edge5]
FEATURE [Part::Chamfer] Chamfer045
  Base = -> Fillet233
  Edges = 1 edges r=1.3: [Edge13]
FEATURE [Part::Chamfer] Chamfer046
  Base = -> Chamfer045
  Edges = 1 edges r=1.3: [Edge16]
FEATURE [Part::Fillet] Fillet234
  Base = -> Box334
  Edges = 2 edges r=0.3: [Edge1,Edge5]
FEATURE [Part::Chamfer] Chamfer047
  Base = -> Fillet234
  Edges = 1 edges r=1.3: [Edge13]
FEATURE [Part::Chamfer] Chamfer048
  Base = -> Chamfer047
  Edges = 1 edges r=1.3: [Edge16]
  Placement = pos=(0.15,0.15,0) rot=(0,0,1;0rad)
FEATURE [Part::Cut] Cut355
  Base = -> Chamfer046
  Tool = -> Chamfer048
FEATURE [Part::Fillet] Fillet235  label="Base_Conector003"
  Base = -> Box336
  Edges = 4 edges r=0.3: [Edge2,Edge4,Edge6,Edge8]
FEATURE [Part::Fillet] Fillet236  label="Base_Conector004"
  Base = -> Box344
  Edges = 4 edges r=0.3: [Edge2,Edge4,Edge6,Edge8]
FEATURE [Part::Fillet] Fillet237  label="Base_Conector005"
  Base = -> Box346
  Edges = 4 edges r=0.3: [Edge2,Edge4,Edge6,Edge8]
  Placement = pos=(10,0,0) rot=(0,0,1;0rad)
FEATURE [Part::MultiFuse] Fusion209  label="Conector_Pines003"
  Placement = pos=(-7,0,52) rot=(0,1,0;3.14159rad)
  Shapes = -> [Box317,Box318,Box319,Array014]
FEATURE [Part::MultiFuse] Fusion210
  Shapes = -> [Cut352,Box316]
FEATURE [Part::MultiFuse] Fusion211  label="Conector_Pines004"
  Placement = pos=(-46.6,0,52) rot=(0,1,0;3.14159rad)
  Shapes = -> [Box321,Box322,Box323,Array015]
FEATURE [Part::MultiFuse] Fusion208  label="PlacaExpansión001"
  Placement = pos=(-1,10,0) rot=(0,0,1;0rad)
  Shapes = -> [Fusion210,Fusion211,Fusion209]
FEATURE [Part::MultiFuse] Fusion212
  Shapes = -> [Box325,Box326]
FEATURE [Part::Fillet] Fillet228
  Base = -> Fusion212
  Edges = 1 edges r=0.2: [Edge6]
FEATURE [Part::Fillet] Fillet229
  Base = -> Fillet228
  Edges = 1 edges r=0.2: [Edge16]
  Placement = pos=(-1.2,0,2) rot=(0,0,1;0rad)
FEATURE [Part::MultiFuse] Fusion213
  Shapes = -> [Box327,Box328]
FEATURE [Part::Fillet] Fillet230
  Base = -> Fusion213
  Edges = 1 edges r=0.2: [Edge6]
FEATURE [Part::Fillet] Fillet231
  Base = -> Fillet230
  Edges = 1 edges r=0.2: [Edge16]
FEATURE [Part::MultiFuse] Fusion214
  Shapes = -> [Fillet231,Fillet229]
FEATURE [Part::FeaturePython] Array016  label="ConexionesPrincipales001"  # Draft array (typed FeaturePython)
  AlwaysSyncPlacement = false
  Angle = 360
  ArrayType = 0
  Axis = (0,0,1)
  Base = -> Fusion214
  Center = (0,0,0)
  Count = 20
  ExpandArray = false
  Fuse = false
  IntervalAxis = (0,0,0)
  IntervalX = (-2.55,0,0)
  IntervalY = (0,100,0)
  IntervalZ = (0,0,100)
  NumberCircles = 3
  NumberPolar = 5
  NumberX = 20
  NumberY = 1
  NumberZ = 1
  Placement = pos=(-2,0,0) rot=(0,0,1;0rad)
  PlacementList = 20 placements: arithmetic series from (0,0,0) step (-2.55,0,0) to (-48.45,0,0)
  RadialDistance = 50
  ScaleList = (20) [(1,1,1),(1,1,1),(1,1,1),(1,1,1),(1,1,1),(1,1,1),(1,1,1),(1,1,1),(1,1,1),(1,1,1),(1,1,1),(1,1,1),(1,1,1),(1,1,1),(1,1,1),(1,1,1),(1,1,1),(1,1,1),+2 more]
  Symmetry = 1
  TangentialDistance = 25
FEATURE [Part::MultiFuse] Fusion215
  Shapes = -> [Box331,Cylinder267,Box332]
FEATURE [Part::Cut] Cut354
  Base = -> Fusion215
  Tool = -> Cylinder268
FEATURE [Part::MultiFuse] Fusion216  label="Conector_Vcc001"
  Placement = pos=(-1,-27,3) rot=(0,0,1;0rad)
  Shapes = -> [Cut354,Fillet232]
FEATURE [Part::MultiFuse] Fusion217  label="Conector_MicroUSB001"
  Placement = pos=(-14,-20.6,2.5) rot=(0,0,1;0rad)
  Shapes = -> [Box335,Cut355]
FEATURE [Part::MultiFuse] Fusion218  label="Conector_Macho_Negro001"
  Shapes = -> [Fillet235,Box337]
FEATURE [Part::FeaturePython] Array018  # Draft array (typed FeaturePython)
  AlwaysSyncPlacement = false
  Angle = 360
  ArrayType = 0
  Axis = (0,0,1)
  Base = -> Fusion218
  Center = (0,0,0)
  Count = 6
  ExpandArray = false
  Fuse = false
  IntervalAxis = (0,0,0)
  IntervalX = (2.4,0,0)
  IntervalY = (0,100,0)
  IntervalZ = (0,0,-2.4)
  NumberCircles = 3
  NumberPolar = 5
  NumberX = 3
  NumberY = 1
  NumberZ = 2
  PlacementList = 6 placements: [(0,0,0),(0,0,-2.4),(2.4,0,0),(2.4,0,-2.4),(4.8,0,0),(4.8,0,-2.4)]
  RadialDistance = 50
  ScaleList = (6) [(1,1,1),(1,1,1),(1,1,1),(1,1,1),(1,1,1),(1,1,1)]
  Symmetry = 1
  TangentialDistance = 25
FEATURE [Part::MultiFuse] Fusion219  label="Conector_MachoAmarillo001"
  Placement = pos=(15,0,0) rot=(0,0,1;0rad)
  Shapes = -> [Box345,Fillet236]
FEATURE [Part::FeaturePython] Array012  # Draft array (typed FeaturePython)
  AlwaysSyncPlacement = false
  Angle = 360
  ArrayType = 0
  Axis = (0,0,1)
  Base = -> Fusion219
  Center = (0,0,0)
  Count = 6
  ExpandArray = false
  Fuse = false
  IntervalAxis = (0,0,0)
  IntervalX = (100,0,0)
  IntervalY = (0,100,0)
  IntervalZ = (0,0,2.4)
  NumberCircles = 3
  NumberPolar = 5
  NumberX = 1
  NumberY = 1
  NumberZ = 6
  PlacementList = 6 placements: arithmetic series from (15,0,0) step (0,0,2.4) to (15,0,12)
  RadialDistance = 50
  ScaleList = (6) [(1,1,1),(1,1,1),(1,1,1),(1,1,1),(1,1,1),(1,1,1)]
  Symmetry = 1
  TangentialDistance = 25
FEATURE [Part::MultiFuse] Fusion220
  Placement = pos=(5,0,17) rot=(0,0,1;0rad)
  Shapes = -> [Fillet237,Box347]
FEATURE [Part::FeaturePython] Array019  # Draft array (typed FeaturePython)
  AlwaysSyncPlacement = false
  Angle = 360
  ArrayType = 0
  Axis = (0,0,1)
  Base = -> Fusion220
  Center = (0,0,0)
  Count = 4
  ExpandArray = false
  Fuse = false
  IntervalAxis = (0,0,0)
  IntervalX = (100,0,0)
  IntervalY = (0,100,0)
  IntervalZ = (0,0,2.4)
  NumberCircles = 3
  NumberPolar = 5
  NumberX = 1
  NumberY = 1
  NumberZ = 4
  PlacementList = 4 placements: arithmetic series from (5,0,17) step (0,0,2.4) to (5,0,24.2)
  RadialDistance = 50
  ScaleList = (4) [(1,1,1),(1,1,1),(1,1,1),(1,1,1)]
  Symmetry = 1
  TangentialDistance = 25
FEATURE [Part::MultiFuse] Fusion221  label="Placaexpansion_Fusionada"
  Shapes = -> [Fusion208,Array016,Array018,Cut353,Cut357,Cut359,Fusion216,Fusion217,Array012,Array019]
